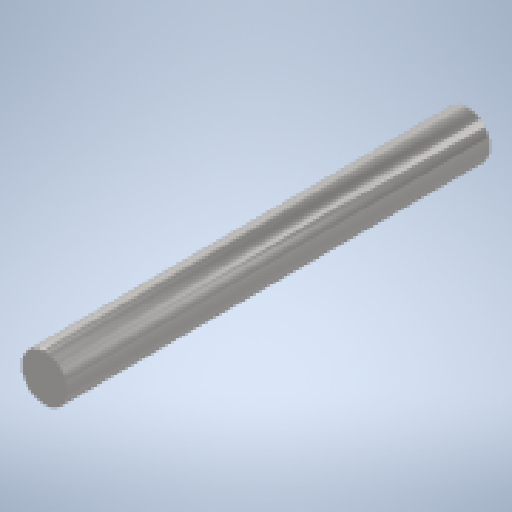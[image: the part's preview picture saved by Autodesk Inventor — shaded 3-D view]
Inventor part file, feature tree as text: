
AUTODESK INVENTOR PART (.ipt)
format: ipt  version: 2023 (Build 270158000, 158)  size: 284,672 bytes
history: mixed  units: in
note: dims shown in document units (in); Inventor stores cm internally (conversion verified against a paired STEP export)
features: sketch x3, extrude x2, chamfer x1, imported_body x1
ambient origin geometry x8: Origin, YZ Plane, XZ Plane, XY Plane, X Axis, Y Axis, Z Axis, Center Point
bodies: Solid1 (imported_parasolid)
feature tree (7):
  extrude  "Extrusion1"  Depth=0.3937in TaperAngle=0.0deg
  extrude  "Extrusion2"  [1 undecoded]
  sketch  "Sketch4"
  sketch  "Sketch1"  dims[d0=5.9055in d1=0.3937in d2=0.0in]
  sketch  "Sketch3"  dims[d3=2.3008in d4=0.0in]
  chamfer  "Chamfer1"  [1 undecoded]
  imported_body  NMx_Import_Brep_tag  [imported B-rep: ~3 faces, bbox_mm=[5.0, 5.0, 91.56]]
note: 2 required parameter values undecoded (feature->parameter linkage not recoverable at this tier; creation-order binding heuristic only, values carry confidence <= 0.55)
